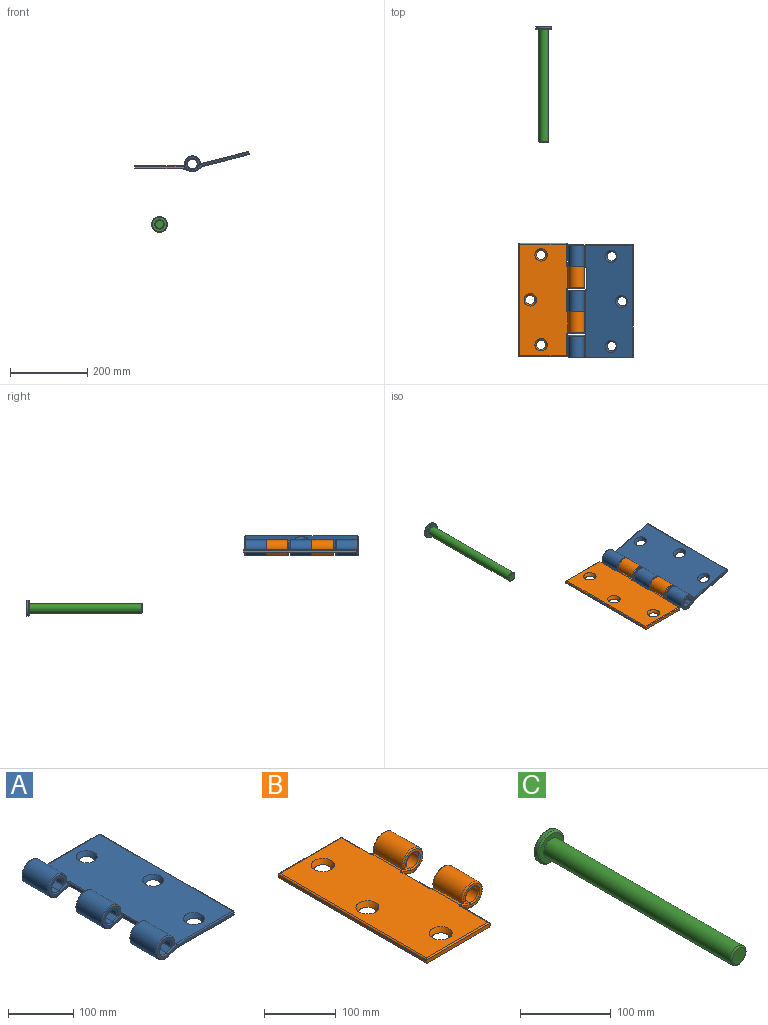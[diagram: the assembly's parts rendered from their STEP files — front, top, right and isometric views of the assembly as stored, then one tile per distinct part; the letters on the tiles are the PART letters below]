
ASSEMBLY  parts=3 mates=1
PART A: 95 faces, bbox 171.6x292.4x44.8 mm
  f0: plane 55.23x16.89mm, normal (0.35,0,-0.94), area 979.8mm2, adj f2,f6,f48,f50,f67,f69
  f1: plane 57.36x19.94mm, normal (-0.32,0,0.95), area 1149.3mm2, adj f10,f13,f36,f38,f40,f57,f59
  f2: plane 288.45x123.49mm, normal (0,0,-1), area 33934.5mm2, adj f0,f3,f4,f20,f21,f22,f47,f49
  f3: plane 54.55x16.89mm, normal (0.35,0,-0.94), area 979.3mm2, adj f2,f5,f45,f47,f77
  f4: plane 55.08x16.89mm, normal (0.35,0,-0.94), area 979.7mm2, adj f2,f15,f66,f68,f87
  f5: cylinder r=20.5mm len=54.4mm, axis (0,1,0), area 5924.3mm2, adj f3,f7,f43,f75
  f6: cylinder r=20.5mm len=54.4mm, axis (0,1,0), area 5924.3mm2, adj f0,f8,f46,f65
  f7: plane 54.4x8.42mm, normal (0,0,-1), area 458.3mm2, adj f5,f9,f41,f73
  f8: plane 54.4x8.42mm, normal (0,0,-1), area 458.3mm2, adj f6,f10,f44,f63
  f9: cylinder r=12.5mm len=54.4mm, axis (0,1,0), area 3708.6mm2, adj f7,f11,f39,f74
  f10: cylinder r=12.5mm len=54.4mm, axis (0,1,0), area 3708.6mm2, adj f1,f8,f42,f61
  f11: plane 55.16x19.94mm, normal (-0.32,0,0.95), area 1146.9mm2, adj f9,f13,f33,f35,f37,f76
  f12: plane 56.6x19.94mm, normal (-0.32,0,0.95), area 1148.6mm2, adj f13,f17,f56,f58,f84
  f13: plane 288.06x123.06mm, normal (0,0,1), area 32879mm2, adj f1,f11,f12,f20,f21,f22,f33,f34
  f14: plane 288x4mm, normal (1,0,0), area 1152mm2, adj f81,f89,f90,f94
  f15: cylinder r=20.5mm len=54.4mm, axis (0,1,0), area 5924.3mm2, adj f4,f16,f64,f83
  f16: plane 54.4x8.42mm, normal (0,0,-1), area 458.3mm2, adj f15,f17,f62,f78
  f17: cylinder r=12.5mm len=54.4mm, axis (0,1,0), area 3708.6mm2, adj f12,f16,f60,f79
  f18: plane 165.48x37mm, normal (0,-1,0), area 911.5mm2, adj f78,f79,f83,f84,f87,f88,f91,f94
  f19: plane 165.48x37mm, normal (0,1,0), area 911.5mm2, adj f73,f74,f75,f76,f77,f80,f81,f82
  f20: cone r=12mm half-angle=26.6deg, axis (0,0,1), area 786.8mm2, adj f2,f13
  f21: cone r=12mm half-angle=26.6deg, axis (0,0,1), area 786.8mm2, adj f2,f13
  f22: cone r=12mm half-angle=26.6deg, axis (0,0,1), area 786.8mm2, adj f2,f13
  f23: plane 54.4x4mm, normal (-1,0,0), area 217.6mm2, adj f31,f32,f34,f51
  f24: plane 40.71x37mm, normal (0,-1,0), area 412.7mm2, adj f31,f37,f39,f41,f43,f45
  f25: plane 40.71x37mm, normal (0,1,0), area 412.7mm2, adj f32,f40,f42,f44,f46,f48
  f26: plane 54.4x4.63mm, normal (-1,0,0), area 251.8mm2, adj f29,f30,f53,f72
  f27: plane 39.56x37mm, normal (0,-1,0), area 408.4mm2, adj f29,f59,f61,f63,f65,f67
  f28: plane 39.56x37mm, normal (0,1,0), area 408.4mm2, adj f30,f58,f60,f62,f64,f66
  f29: cylinder r=2mm len=5.26mm, axis (0,0,-1), area 12.7mm2, adj f26,f27,f55,f57,f69,f71
  f30: cylinder r=2mm len=5.26mm, axis (0,0,1), area 12.7mm2, adj f26,f28,f54,f56,f68,f70
  f31: cylinder r=2mm len=4.52mm, axis (0,0,-1), area 12.4mm2, adj f23,f24,f33,f35,f47,f49
  f32: cylinder r=2mm len=4.52mm, axis (0,0,1), area 12.4mm2, adj f23,f25,f36,f38,f50,f52
  f33: torus R=4mm, axis (0,0,-1), area 9.3mm2, adj f11,f13,f31,f34,f35
  f34: cylinder r=2mm len=54.4mm, axis (0,-1,0), area 170.9mm2, adj f13,f23,f33,f36
  f35: bspline ~2.7x2.38mm, area 5.5mm2, adj f11,f31,f33,f37
  f36: torus R=4mm, axis (0,0,-1), area 9.3mm2, adj f1,f13,f32,f34,f38
  f37: cylinder r=2mm len=18.16mm, axis (0.95,0,0.32), area 58.1mm2, adj f11,f24,f35,f39
  f38: bspline ~2.7x2.38mm, area 5.5mm2, adj f1,f32,f36,f40
  f39: torus R=14.5mm, axis (0,-1,0), area 222.3mm2, adj f9,f24,f37,f41
  f40: cylinder r=2mm len=18.16mm, axis (-0.95,0,-0.32), area 58.1mm2, adj f1,f25,f38,f42
  f41: cylinder r=2mm len=8.42mm, axis (-1,0,0), area 19.6mm2, adj f7,f24,f39,f43
  f42: torus R=14.5mm, axis (0,-1,0), area 222.3mm2, adj f10,f25,f40,f44
  f43: torus R=18.5mm, axis (0,-1,0), area 327.5mm2, adj f5,f24,f41,f45
  f44: cylinder r=2mm len=8.42mm, axis (1,0,0), area 19.6mm2, adj f8,f25,f42,f46
  f45: cylinder r=2mm len=16.49mm, axis (-0.94,0,-0.35), area 52.9mm2, adj f3,f24,f43,f47
  f46: torus R=18.5mm, axis (0,-1,0), area 327.5mm2, adj f6,f25,f44,f48
  f47: bspline ~2.4x2.13mm, area 2.8mm2, adj f2,f3,f31,f45,f49
  f48: cylinder r=2mm len=16.49mm, axis (0.94,0,0.35), area 52.9mm2, adj f0,f25,f46,f50
  f49: torus R=4mm, axis (0,0,1), area 9.7mm2, adj f2,f31,f47,f51
  f50: bspline ~2.4x2.13mm, area 2.8mm2, adj f0,f2,f32,f48,f52
  f51: cylinder r=2mm len=54.4mm, axis (0,1,0), area 170.9mm2, adj f2,f23,f49,f52
  f52: torus R=4mm, axis (0,0,1), area 9.7mm2, adj f2,f32,f50,f51
  f53: cylinder r=2mm len=54.4mm, axis (0,-1,0), area 109.1mm2, adj f13,f26,f54,f55
  f54: bspline ~2.37x1.92mm, area 2.8mm2, adj f13,f30,f53,f56
  f55: bspline ~2.37x1.92mm, area 2.8mm2, adj f13,f29,f53,f57
  f56: bspline ~3.57x3.12mm, area 9.3mm2, adj f12,f30,f54,f58
  f57: bspline ~3.94x3.32mm, area 9.3mm2, adj f1,f29,f55,f59
  f58: cylinder r=2mm len=17.01mm, axis (-0.95,0,-0.32), area 54.3mm2, adj f12,f28,f56,f60
  f59: cylinder r=2mm len=17.01mm, axis (0.95,0,0.32), area 54.3mm2, adj f1,f27,f57,f61
  f60: torus R=14.5mm, axis (0,-1,0), area 222.3mm2, adj f17,f28,f58,f62
  f61: torus R=14.5mm, axis (0,-1,0), area 222.3mm2, adj f10,f27,f59,f63
  f62: cylinder r=2mm len=8.42mm, axis (1,0,0), area 19.6mm2, adj f16,f28,f60,f64
  f63: cylinder r=2mm len=8.42mm, axis (-1,0,0), area 19.6mm2, adj f8,f27,f61,f65
  f64: torus R=18.5mm, axis (0,-1,0), area 327.5mm2, adj f15,f28,f62,f66
  f65: torus R=18.5mm, axis (0,-1,0), area 327.5mm2, adj f6,f27,f63,f67
  f66: cylinder r=2mm len=15.35mm, axis (0.94,0,0.35), area 49.1mm2, adj f4,f28,f64,f68
  f67: cylinder r=2mm len=15.35mm, axis (-0.94,0,-0.35), area 49.1mm2, adj f0,f27,f65,f69
  f68: bspline ~3.61x3.08mm, area 5.9mm2, adj f4,f30,f66,f70
  f69: bspline ~3.61x3.08mm, area 5.9mm2, adj f0,f29,f67,f71
  f70: bspline ~3.87x2.48mm, area 5.3mm2, adj f2,f30,f68,f72
  f71: bspline ~3.87x2.48mm, area 5.3mm2, adj f2,f29,f69,f72
  f72: cylinder r=2mm len=54.4mm, axis (0,1,0), area 109.1mm2, adj f2,f26,f70,f71
  f73: cylinder r=2mm len=8.42mm, axis (-1,0,0), area 19.6mm2, adj f7,f19,f74,f75
  f74: torus R=14.5mm, axis (0,-1,0), area 222.3mm2, adj f9,f19,f73,f76
  f75: torus R=18.5mm, axis (0,-1,0), area 327.5mm2, adj f5,f19,f73,f77
  f76: cylinder r=2mm len=20.58mm, axis (0.95,0,0.32), area 65.7mm2, adj f11,f19,f74,f80
  f77: cylinder r=2mm len=17.91mm, axis (-0.94,0,-0.35), area 57.1mm2, adj f3,f19,f75,f82
  f78: cylinder r=2mm len=8.42mm, axis (1,0,0), area 19.6mm2, adj f16,f18,f79,f83
  f79: torus R=14.5mm, axis (0,-1,0), area 222.3mm2, adj f17,f18,f78,f84
  f80: cylinder r=2mm len=123mm, axis (1,0,0), area 385.9mm2, adj f13,f19,f76,f85
  f81: cylinder r=2mm len=4mm, axis (0,0,-1), area 12.6mm2, adj f14,f19,f85,f86
  f82: cylinder r=2mm len=123.36mm, axis (-1,0,0), area 387mm2, adj f2,f19,f77,f86
  f83: torus R=18.5mm, axis (0,-1,0), area 327.5mm2, adj f15,f18,f78,f87
  f84: cylinder r=2mm len=20.58mm, axis (-0.95,0,-0.32), area 65.7mm2, adj f12,f18,f79,f88
  f85: sphere r=2mm, area 6.3mm2, adj f80,f81,f89
  f86: sphere r=2mm, area 4mm2, adj f81,f82,f90
  f87: cylinder r=2mm len=17.91mm, axis (0.94,0,0.35), area 57.1mm2, adj f4,f18,f83,f91
  f88: cylinder r=2mm len=123mm, axis (-1,0,0), area 385.9mm2, adj f13,f18,f84,f92
  f89: cylinder r=2mm len=288mm, axis (0,1,0), area 904.8mm2, adj f13,f14,f85,f92
  f90: cylinder r=2mm len=288mm, axis (0,1,0), area 904.8mm2, adj f2,f14,f86,f93
  f91: cylinder r=2mm len=123.36mm, axis (1,0,0), area 387mm2, adj f2,f18,f87,f93
  f92: sphere r=2mm, area 6.3mm2, adj f88,f89,f94
  f93: sphere r=2mm, area 6.3mm2, adj f90,f91,f94
  f94: cylinder r=2mm len=4mm, axis (0,0,1), area 12.6mm2, adj f14,f18,f92,f93
PART B: 76 faces, bbox 171.2x292x44.4 mm
  f0: plane 54.84x16.89mm, normal (-0.35,0,-0.94), area 979.4mm2, adj f2,f12,f54,f55,f73,f75
  f1: plane 54.84x16.89mm, normal (-0.35,0,-0.94), area 979.4mm2, adj f3,f12,f31,f32,f66,f68
  f2: cylinder r=20.5mm len=54.4mm, axis (0,1,0), area 5924.3mm2, adj f0,f4,f52,f71
  f3: cylinder r=20.5mm len=54.4mm, axis (0,1,0), area 5924.3mm2, adj f1,f5,f33,f64
  f4: plane 54.4x8.42mm, normal (0,0,-1), area 458.3mm2, adj f2,f6,f50,f69
  f5: plane 54.4x8.42mm, normal (0,0,-1), area 458.3mm2, adj f3,f7,f34,f62
  f6: cylinder r=12.5mm len=54.4mm, axis (0,1,0), area 3708.6mm2, adj f4,f8,f48,f67
  f7: cylinder r=12.5mm len=54.4mm, axis (0,1,0), area 3708.6mm2, adj f5,f9,f35,f60
  f8: plane 56.23x19.94mm, normal (0.32,0,0.95), area 1148mm2, adj f6,f13,f44,f45,f46,f61,f63,f65
  f9: plane 56.23x19.94mm, normal (0.32,0,0.95), area 1148mm2, adj f7,f13,f36,f37,f38,f56,f57,f58
  f10: plane 125x6mm, normal (0,-1,0), area 748.3mm2, adj f11,f12,f19,f29,f40,f47
  f11: plane 292x4mm, normal (-1,0,0), area 1168mm2, adj f10,f14,f41,f47
  f12: plane 290x123.06mm, normal (0,0,-1), area 33962.8mm2, adj f0,f1,f10,f15,f16,f17,f29,f30
  f13: plane 288x123mm, normal (0,0,1), area 32665.2mm2, adj f8,f9,f15,f16,f17,f38,f39,f40
  f14: plane 125x4mm, normal (0,1,0), area 500mm2, adj f11,f24,f42,f49
  f15: cone r=12mm half-angle=26.6deg, axis (0,0,1), area 786.8mm2, adj f12,f13
  f16: cone r=12mm half-angle=26.6deg, axis (0,0,1), area 786.8mm2, adj f12,f13
  f17: cone r=12mm half-angle=26.6deg, axis (0,0,1), area 786.8mm2, adj f12,f13
  f18: plane 40.48x37mm, normal (0,-1,0), area 411.9mm2, adj f25,f32,f33,f34,f35,f36
  f19: plane 56.4x4mm, normal (1,0,0), area 225.6mm2, adj f10,f25,f29,f39
  f20: plane 40.48x37mm, normal (0,-1,0), area 411.9mm2, adj f26,f65,f67,f69,f71,f73
  f21: plane 40.48x37mm, normal (0,1,0), area 411.9mm2, adj f27,f58,f60,f62,f64,f66
  f22: plane 54.4x4mm, normal (1,0,0), area 217.6mm2, adj f26,f27,f59,f72
  f23: plane 40.48x37mm, normal (0,1,0), area 411.9mm2, adj f28,f46,f48,f50,f52,f54
  f24: plane 56.4x4mm, normal (1,0,0), area 225.6mm2, adj f14,f28,f43,f51
  f25: cylinder r=2mm len=4.61mm, axis (0,0,-1), area 12.3mm2, adj f18,f19,f30,f31,f37,f38
  f26: cylinder r=2mm len=4.61mm, axis (0,0,-1), area 12.3mm2, adj f20,f22,f61,f63,f74,f75
  f27: cylinder r=2mm len=4.61mm, axis (0,0,1), area 12.3mm2, adj f21,f22,f56,f57,f68,f70
  f28: cylinder r=2mm len=4.61mm, axis (0,0,1), area 12.3mm2, adj f23,f24,f44,f45,f53,f55
  f29: cylinder r=2mm len=56.4mm, axis (0,-1,0), area 177.2mm2, adj f10,f12,f19,f30
  f30: torus R=4mm, axis (0,0,1), area 9.2mm2, adj f12,f25,f29,f31
  f31: bspline ~2.48x2.34mm, area 3.4mm2, adj f1,f12,f25,f30,f32
  f32: cylinder r=2mm len=16.27mm, axis (-0.94,0,0.35), area 52.2mm2, adj f1,f18,f31,f33
  f33: torus R=18.5mm, axis (0,1,0), area 327.5mm2, adj f3,f18,f32,f34
  f34: cylinder r=2mm len=8.42mm, axis (-1,0,0), area 19.6mm2, adj f5,f18,f33,f35
  f35: torus R=14.5mm, axis (0,1,0), area 222.3mm2, adj f7,f18,f34,f36
  f36: cylinder r=2mm len=17.94mm, axis (0.95,0,-0.32), area 57.4mm2, adj f9,f18,f35,f37
  f37: bspline ~2.77x2.55mm, area 6mm2, adj f9,f25,f36,f38
  f38: torus R=4mm, axis (0,0,-1), area 8.7mm2, adj f9,f13,f25,f37,f39
  f39: cylinder r=2mm len=56.4mm, axis (0,-1,0), area 174mm2, adj f13,f19,f38,f40
  f40: cylinder r=2mm len=125mm, axis (1,0,0), area 386.4mm2, adj f10,f13,f39,f41
  f41: cylinder r=2mm len=292mm, axis (0,1,0), area 911.1mm2, adj f11,f13,f40,f42
  f42: cylinder r=2mm len=125mm, axis (-1,0,0), area 386.4mm2, adj f13,f14,f41,f43
  f43: cylinder r=2mm len=56.4mm, axis (0,1,0), area 174mm2, adj f13,f24,f42,f44
  f44: torus R=4mm, axis (0,0,-1), area 8.7mm2, adj f8,f13,f28,f43,f45
  f45: bspline ~3.65x3.14mm, area 6mm2, adj f8,f28,f44,f46
  f46: cylinder r=2mm len=17.94mm, axis (-0.95,0,0.32), area 57.4mm2, adj f8,f23,f45,f48
  f47: cylinder r=2mm len=292mm, axis (0,1,0), area 914.2mm2, adj f10,f11,f12,f49
  f48: torus R=14.5mm, axis (0,1,0), area 222.3mm2, adj f6,f23,f46,f50
  f49: cylinder r=2mm len=125mm, axis (1,0,0), area 386.4mm2, adj f12,f14,f47,f51
  f50: cylinder r=2mm len=8.42mm, axis (1,0,0), area 19.6mm2, adj f4,f23,f48,f52
  f51: cylinder r=2mm len=56.4mm, axis (0,-1,0), area 174mm2, adj f12,f24,f49,f53
  f52: torus R=18.5mm, axis (0,1,0), area 327.5mm2, adj f2,f23,f50,f54
  f53: torus R=4mm, axis (0,0,1), area 9.2mm2, adj f12,f28,f51,f55
  f54: cylinder r=2mm len=16.27mm, axis (0.94,0,-0.35), area 52.2mm2, adj f0,f23,f52,f55
  f55: bspline ~2.48x2.34mm, area 3.4mm2, adj f0,f12,f28,f53,f54
  f56: bspline ~3.65x3.14mm, area 6mm2, adj f9,f27,f57,f58
  f57: torus R=4mm, axis (0,0,-1), area 8.7mm2, adj f9,f13,f27,f56,f59
  f58: cylinder r=2mm len=17.94mm, axis (-0.95,0,0.32), area 57.4mm2, adj f9,f21,f56,f60
  f59: cylinder r=2mm len=54.4mm, axis (0,-1,0), area 170.9mm2, adj f13,f22,f57,f61
  f60: torus R=14.5mm, axis (0,1,0), area 222.3mm2, adj f7,f21,f58,f62
  f61: torus R=4mm, axis (0,0,-1), area 8.7mm2, adj f8,f13,f26,f59,f63
  f62: cylinder r=2mm len=8.42mm, axis (1,0,0), area 19.6mm2, adj f5,f21,f60,f64
  f63: bspline ~3.65x3.14mm, area 6mm2, adj f8,f26,f61,f65
  f64: torus R=18.5mm, axis (0,1,0), area 327.5mm2, adj f3,f21,f62,f66
  f65: cylinder r=2mm len=17.94mm, axis (0.95,0,-0.32), area 57.4mm2, adj f8,f20,f63,f67
  f66: cylinder r=2mm len=16.27mm, axis (0.94,0,-0.35), area 52.2mm2, adj f1,f21,f64,f68
  f67: torus R=14.5mm, axis (0,1,0), area 222.3mm2, adj f6,f20,f65,f69
  f68: bspline ~2.48x2.34mm, area 3.4mm2, adj f1,f12,f27,f66,f70
  f69: cylinder r=2mm len=8.42mm, axis (-1,0,0), area 19.6mm2, adj f4,f20,f67,f71
  f70: torus R=4mm, axis (0,0,1), area 9.2mm2, adj f12,f27,f68,f72
  f71: torus R=18.5mm, axis (0,1,0), area 327.5mm2, adj f2,f20,f69,f73
  f72: cylinder r=2mm len=54.4mm, axis (0,-1,0), area 170.9mm2, adj f12,f22,f70,f74
  f73: cylinder r=2mm len=16.27mm, axis (-0.94,0,0.35), area 52.2mm2, adj f0,f20,f71,f75
  f74: torus R=4mm, axis (0,0,1), area 9.2mm2, adj f12,f26,f72,f75
  f75: bspline ~2.48x2.34mm, area 3.4mm2, adj f0,f12,f26,f73,f74
PART C: 8 faces, bbox 44.4x300x44.4 mm
  f0: cylinder r=12.25mm len=290mm, axis (0,1,0), area 22321mm2, adj f4,f7
  f1: plane 20.5x20.5mm, normal (0,-1,0), area 330.1mm2, adj f7
  f2: cylinder r=20.5mm len=41mm, axis (0,-1,0), area 515.2mm2, adj f5,f6
  f3: plane 37x37mm, normal (0,1,0), area 1075.2mm2, adj f6
  f4: plane 37x37mm, normal (0,-1,0), area 603.8mm2, adj f0,f5
  f5: torus R=18.5mm, axis (0,1,0), area 390.3mm2, adj f2,f4
  f6: torus R=18.5mm, axis (0,1,0), area 390.3mm2, adj f2,f3
  f7: torus R=10.25mm, axis (0,1,0), area 227.5mm2, adj f0,f1
PLACE A rot(axis=(0,-1,0),14.3deg) t=(-42.35,-31.15,-9.22)mm
PLACE B t=(-43.34,-27.15,-3.19)mm fixed
PLACE C rot(axis=(0,-1,0),81.9deg) t=(-102.5,525.92,-179.82)mm
MATE revolute A.f42 <-> B.f2  axis (0,-1,0) through (-19.35,-204.35,1.81)mm
